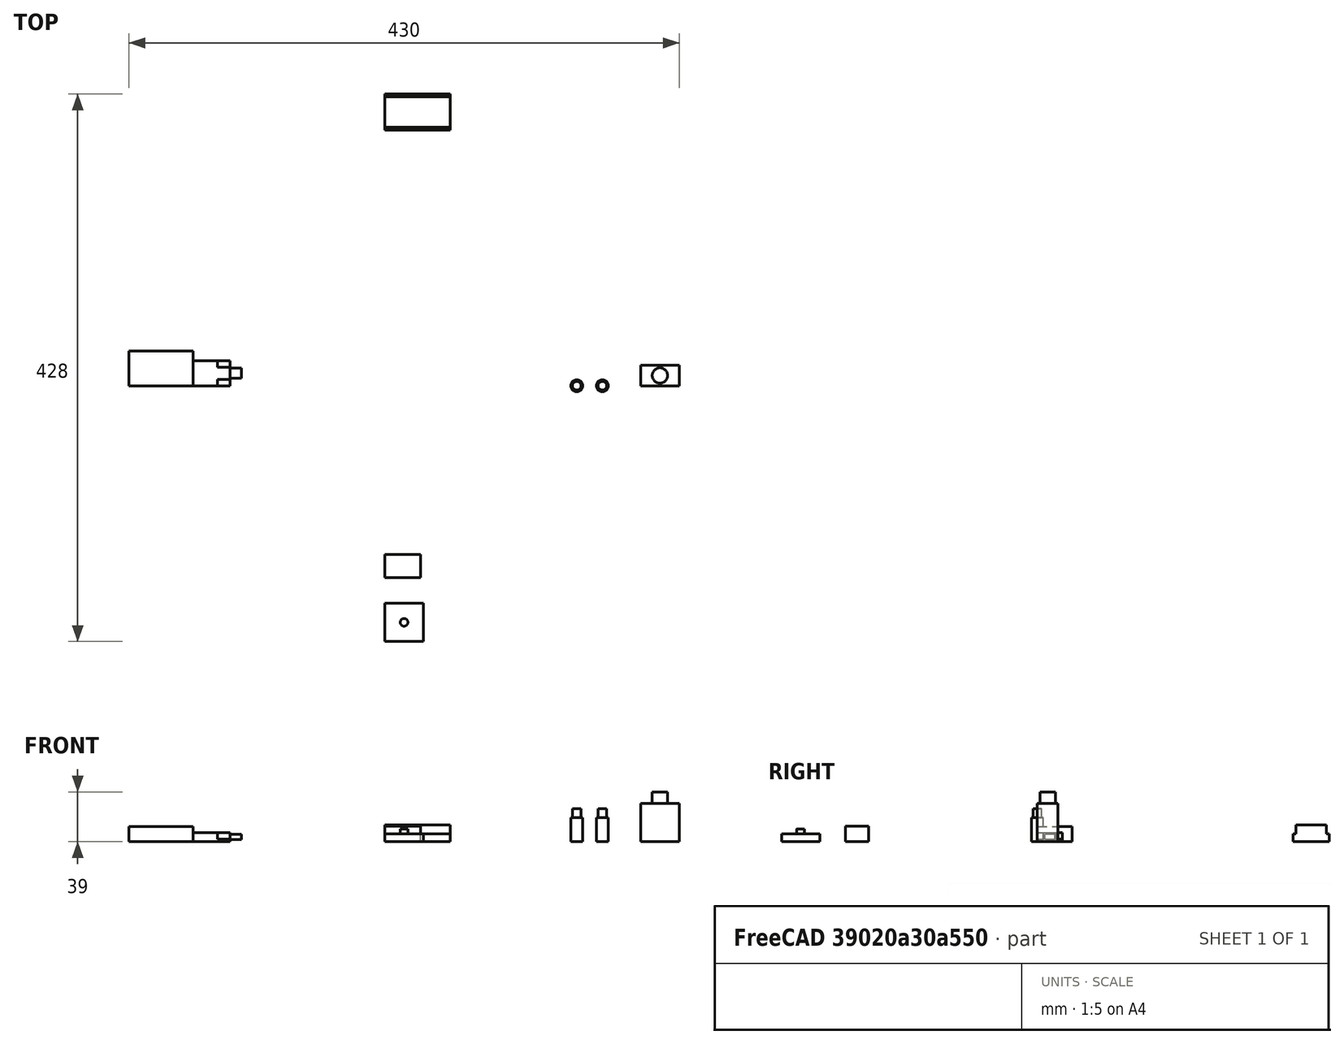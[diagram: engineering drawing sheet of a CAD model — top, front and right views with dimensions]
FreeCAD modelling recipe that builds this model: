
FCSTD DOCUMENT  (FreeCAD 0.19R)
Label: RoundTimer
License: All rights reserved
LicenseURL: http://en.wikipedia.org/wiki/All_rights_reserved
objects: Part::Box×10, Part::Cylinder×6, Part::MultiFuse×4, Part::Fuse×2, Part::Cut×2
note: 24 computed .brp shape members not serialized (recipe doc carries the construction recipe); baked Part::Feature solids carry a one-line shape summary decoded from their .brp

FEATURE [Part::Box] Box  label="Cube"
  AttacherType = Attacher::AttachEngine3D
  Height = 30
  Length = 30
  Width = 16
FEATURE [Part::Cylinder] Cylinder
  Angle = 360
  AttacherType = Attacher::AttachEngine3D
  Height = 9
  Placement = pos=(15,8,30) rot=(0,0,1;0rad)
  Radius = 6
FEATURE [Part::Fuse] Fusion  label="Awesome switch"
  Base = -> Box
  Placement = pos=(200,0,0) rot=(0,0,1;0rad)
  Tool = -> Cylinder
FEATURE [Part::Box] Box001  label="Cube001"
  AttacherType = Attacher::AttachEngine3D
  Height = 6
  Length = 51
  Width = 28
FEATURE [Part::Box] Box002  label="Cube002"
  AttacherType = Attacher::AttachEngine3D
  Height = 7
  Length = 51
  Placement = pos=(0,2,6) rot=(0,0,1;0rad)
  Width = 24
FEATURE [Part::MultiFuse] Fusion001  label="LCD Display"
  Placement = pos=(0,200,0) rot=(0,0,1;0rad)
  Shapes = -> [Box001,Box002]
FEATURE [Part::Box] Box003  label="Lipo Battery"
  AttacherType = Attacher::AttachEngine3D
  Height = 12
  Length = 50
  Placement = pos=(-200,0,0) rot=(0,0,1;0rad)
  Width = 27
FEATURE [Part::Cylinder] Cylinder001
  Angle = 360
  AttacherType = Attacher::AttachEngine3D
  Height = 19
  Radius = 4.65
FEATURE [Part::Cylinder] Cylinder002
  Angle = 360
  AttacherType = Attacher::AttachEngine3D
  Height = 6.7
  Placement = pos=(0,0,19) rot=(0,0,1;0rad)
  Radius = 3.35
FEATURE [Part::MultiFuse] Fusion002  label="Push Button mode/reset"
  Placement = pos=(150,0,0) rot=(0,0,1;0rad)
  Shapes = -> [Cylinder001,Cylinder002]
FEATURE [Part::Cylinder] Cylinder003
  Angle = 360
  AttacherType = Attacher::AttachEngine3D
  Height = 19
  Radius = 4.65
FEATURE [Part::Cylinder] Cylinder004
  Angle = 360
  AttacherType = Attacher::AttachEngine3D
  Height = 6.7
  Placement = pos=(0,0,19) rot=(0,0,1;0rad)
  Radius = 3.35
FEATURE [Part::MultiFuse] Fusion003  label="Push Button start/stop"
  Placement = pos=(170,0,0) rot=(0,0,1;0rad)
  Shapes = -> [Cylinder003,Cylinder004]
FEATURE [Part::Box] Box004  label="Cube003"
  AttacherType = Attacher::AttachEngine3D
  Height = 7.25
  Length = 29
  Width = 19.5
FEATURE [Part::Box] Box005  label="Cube004"
  AttacherType = Attacher::AttachEngine3D
  Height = 4
  Length = 10
  Placement = pos=(28,5.75,1.75) rot=(0,0,1;0rad)
  Width = 8
FEATURE [Part::Box] Box006  label="Cube005"
  AttacherType = Attacher::AttachEngine3D
  Height = 10
  Length = 10
  Placement = pos=(19,-5,2) rot=(0,0,1;0rad)
  Width = 10
FEATURE [Part::MultiFuse] Fusion004
  Shapes = -> [Box004,Box005]
FEATURE [Part::Cut] Cut
  Base = -> Fusion004
  Tool = -> Box006
FEATURE [Part::Box] Box007  label="Cube006"
  AttacherType = Attacher::AttachEngine3D
  Height = 10
  Length = 10
  Placement = pos=(19,14.5,2) rot=(0,0,1;0rad)
  Width = 10
FEATURE [Part::Cut] Cut001  label="USB Battery Charger"
  Base = -> Cut
  Placement = pos=(-150,0,0) rot=(0,0,1;0rad)
  Tool = -> Box007
FEATURE [Part::Box] Box008  label="Piezo Driver"
  AttacherType = Attacher::AttachEngine3D
  Height = 12.2
  Length = 28
  Placement = pos=(0,-150,0) rot=(0,0,1;0rad)
  Width = 18
FEATURE [Part::Box] Box009  label="Cube007"
  AttacherType = Attacher::AttachEngine3D
  Height = 6
  Length = 30
  Width = 30
FEATURE [Part::Cylinder] Cylinder005
  Angle = 360
  AttacherType = Attacher::AttachEngine3D
  Height = 10
  Placement = pos=(15,15,0) rot=(0,0,1;0rad)
  Radius = 3
FEATURE [Part::Fuse] Fusion005  label="Piezo Buzzer"
  Base = -> Box009
  Placement = pos=(0,-200,0) rot=(0,0,1;0rad)
  Tool = -> Cylinder005
